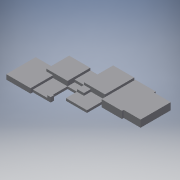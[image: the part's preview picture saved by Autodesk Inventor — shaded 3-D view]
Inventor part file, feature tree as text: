
AUTODESK INVENTOR PART (.ipt)
format: ipt  version: 2018.3 (Build 223284000, 284)  size: 216,064 bytes
history: native  units: mm
features: extrude x13, sketch x13
ambient origin geometry x8: Origin, YZ Plane, XZ Plane, XY Plane, X Axis, Y Axis, Z Axis, Center Point
bodies: Solid1 (feature_tree)
feature tree (26):
  extrude  "Extrusion1"  Depth=44.9mm
  extrude  "Extrusion2"  Depth=2.33mm
  extrude  "Extrusion3"  Depth=32.05mm
  extrude  "Extrusion4"  Depth=31.18mm TaperAngle=0.0deg
  extrude  "Extrusion5"  Depth=6.86mm TaperAngle=0.0deg
  extrude  "Extrusion6"  Depth=24.01mm TaperAngle=0.0deg
  extrude  "Extrusion7"  Depth=9.35mm
  extrude  "Extrusion8"  Depth=27.44mm
  extrude  "Extrusion9"  Depth=6.24mm
  extrude  "Extrusion10"  Depth=6.24mm TaperAngle=0.0deg
  extrude  "Extrusion11"  Depth=39.29mm
  extrude  "Extrusion12"  Depth=8.73mm TaperAngle=0.0deg
  extrude  "Extrusion13"  Depth=19.33mm TaperAngle=0.0deg
  sketch  "Sketch1"  dims[d0=49.58mm d1=44.9mm]
  sketch  "Sketch2"  dims[d2=22.45mm d3=2.33mm]
  sketch  "Sketch3"  dims[d4=9.35mm d5=0.0mm d6=32.05mm]
  sketch  "Sketch4"  dims[d7=5.16mm d8=31.18mm d9=0.0mm]
  sketch  "Sketch5"  dims[d10=3.12mm d11=0.0mm d12=6.86mm d13=0.0mm]
  sketch  "Sketch6"  dims[d14=3.12mm d15=24.01mm d16=0.0mm]
  sketch  "Sketch7"  dims[d17=9.35mm d18=9.35mm]
  sketch  "Sketch8"  dims[d19=3.12mm d20=0.0mm d21=27.44mm]
  sketch  "Sketch9"  dims[d22=12.47mm d23=0.0mm d24=6.24mm]
  sketch  "Sketch10"  dims[d25=3.12mm d26=6.24mm d27=0.0mm]
  sketch  "Sketch11"  dims[d28=28.06mm d29=0.0mm d30=39.29mm]
  sketch  "Sketch12"  dims[d31=23.7mm d32=0.0mm d33=8.73mm d34=0.0mm]
  sketch  "Sketch13"  dims[d35=26.82mm d36=19.33mm d37=0.0mm d38=6.24mm d39=4.37mm d40=4.37mm d41=0.0mm]
